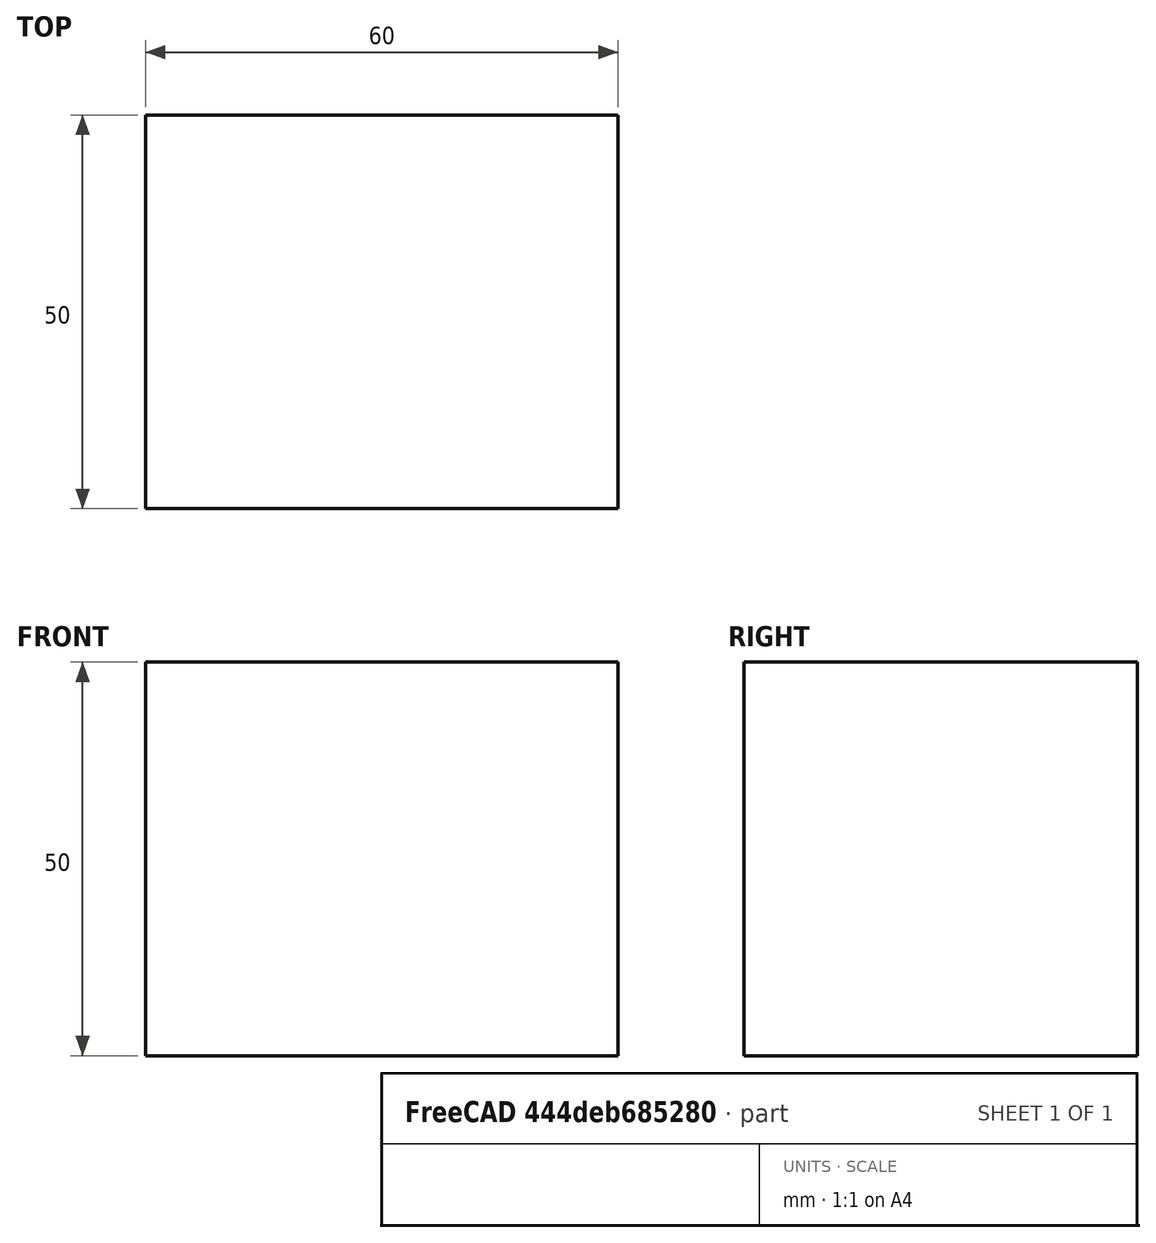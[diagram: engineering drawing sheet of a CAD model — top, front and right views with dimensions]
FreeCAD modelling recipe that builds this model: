
FCSTD DOCUMENT  (FreeCAD 0.15R4671 (Git))
Label: Flat Bar 60x50 EN10058 S235JR
License: All rights reserved
LicenseURL: http://en.wikipedia.org/wiki/All_rights_reserved
objects: Sketcher::SketchObject×1, Part::Extrusion×1
note: 2 computed .brp shape members not serialized (recipe doc carries the construction recipe); baked Part::Feature solids carry a one-line shape summary decoded from their .brp

FEATURE [Sketcher::SketchObject] Sketch
  sketch-geometry (4):
    g0: LineSegment StartX=-30 StartY=-25 StartZ=0 EndX=30 EndY=-25 EndZ=0
    g1: LineSegment StartX=30 StartY=-25 StartZ=0 EndX=30 EndY=25 EndZ=0
    g2: LineSegment StartX=30 StartY=25 StartZ=0 EndX=-30 EndY=25 EndZ=0
    g3: LineSegment StartX=-30 StartY=25 StartZ=0 EndX=-30 EndY=-25 EndZ=0
  constraints (12):
    c: Coincident(g0,g1)
    c: Coincident(g1,g2)
    c: Coincident(g2,g3)
    c: Coincident(g3,g0)
    c: Horizontal(g0)
    c: Horizontal(g2)
    c: Vertical(g1)
    c: Vertical(g3)
    c: Symmetric(g1,g2,g-2)
    c: Symmetric(g0,g1,g-1)
    c: DistanceY(g1) = 50
    c: DistanceX(g0) = 60
FEATURE [Part::Extrusion] Extrude  label="Flat Bar 60x50 EN10058 S235JR"
  Base = -> Sketch
  Dir = (0,0,50)
  Solid = true
